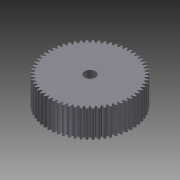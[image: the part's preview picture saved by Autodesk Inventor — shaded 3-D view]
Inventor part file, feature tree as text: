
AUTODESK INVENTOR PART (.ipt)
format: ipt  version: 2011 (Build 150239000, 239)  size: 352,256 bytes
history: native  units: mm (DEFAULTED — no unit token found)
features: plane x3, other x3, sketch x2, extrude x1, hole x1
ambient origin geometry x8: Origin, YZ Plane, XZ Plane, XY Plane, X Axis, Y Axis, Z Axis, Center Point
bodies: Solid1 (feature_tree)
feature tree (10):
  extrude  "Extrusion1"  Depth=5.0mm TaperAngle=0.0deg
  plane  "Work Plane2"
  plane  "Work Plane8"
  plane  "Work Plane9"
  other  "Spur Gear"
  hole  "Hole1"  [1 undecoded]
  sketch  "Sketch1"  dims[d0=15.5mm d1=5.0mm d2=0.0mm]
  sketch  "Sketch2"  dims[d3=15.0mm d4=10.0mm d5=0.0mm d16=10.0mm d17=0.0mm d34=0.523599mm d39=0.0mm d41=0.0mm d43=10.0mm d46=10.0mm d47=0.0mm d48=0.0mm d49=10.0mm d50=10.0mm d51=2.0mm d52=6.0mm d53=4.0mm d54=2.0mm d55=90.0deg d56=8.0mm d57=20.594885mm]
  other  "Srf1"
  other  "Pitch Diameter"
note: 1 required parameter value undecoded (feature->parameter linkage not recoverable at this tier; creation-order binding heuristic only, values carry confidence <= 0.55)
